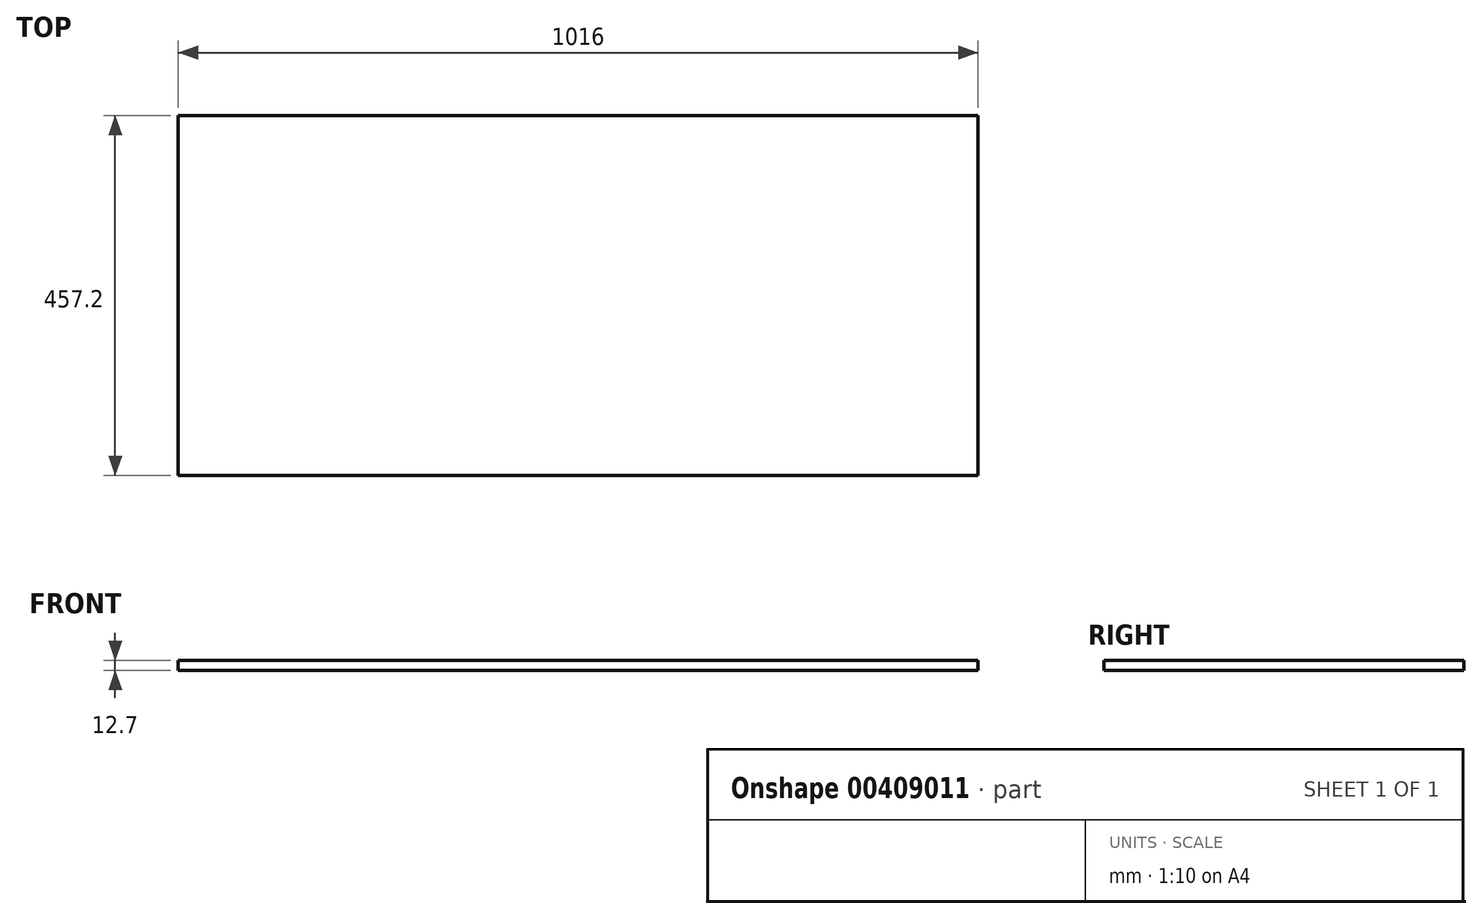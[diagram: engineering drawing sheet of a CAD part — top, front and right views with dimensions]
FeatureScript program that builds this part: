
annotation { "Feature Type Name" : "Feature", "Feature Type Description" : "" }
export const myFeature = defineFeature(function(context is Context, id is Id, definition is map)
    precondition{}
    {
        {
            var Q0;
            Q0=qCreatedBy(makeId("Top.planeOp"),FACE);
            var sketch = newSketch(context, id + "F0", { "sketchPlane" : qUnion([Q0])});
            skLineSegment(sketch, "E0.bottom", {"start": v(-508, 228.6) * mm, "end": v(508, 228.6) * mm});
            skLineSegment(sketch, "E0.top", {"start": v(-508, -228.6) * mm, "end": v(508, -228.6) * mm});
            skLineSegment(sketch, "E0.left", {"start": v(-508, 228.6) * mm, "end": v(-508, -228.6) * mm});
            skLineSegment(sketch, "E0.right", {"start": v(508, 228.6) * mm, "end": v(508, -228.6) * mm});
            skPoint(sketch, "E0.middle", {"position": v(0, 0) * mm});
            skSolve(sketch);
        }
        {
            var Q0;
            Q0=makeQuery(id+"F0.imprint","IMPRINT",FACE,{"disambiguationData":[TD([[makeQuery(id+"F0.imprint","IMPRINT",EDGE,{"derivedFrom":sQuery(id+"F0.wireOp",EDGE,"E0.bottom")}),-1.0]])]});
            extrude(context, id + "F1", {"entities" : qUnion([Q0]), "depth" : 12.7 * mm});
        }
    });
